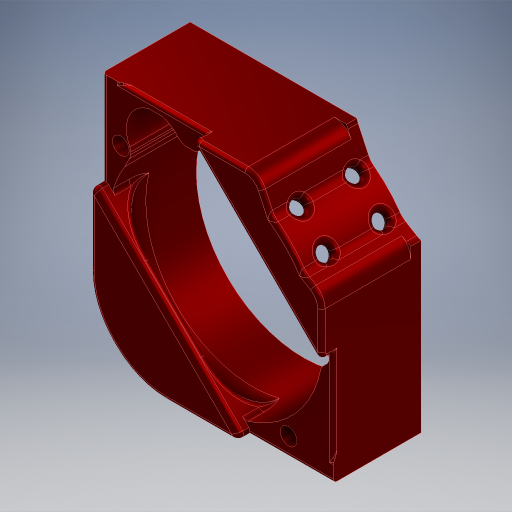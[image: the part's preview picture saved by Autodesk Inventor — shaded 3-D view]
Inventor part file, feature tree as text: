
AUTODESK INVENTOR PART (.ipt)
format: ipt  version: 2024.2 (Build 282272000, 272)  size: 4,199,424 bytes
history: native  units: in
note: dims shown in document units (in); Inventor stores cm internally (conversion verified against a paired STEP export)
features: extrude x10, sketch x10, fillet x3, projected_geometry x1
ambient origin geometry x8: Origin, YZ Plane, XZ Plane, XY Plane, X Axis, Y Axis, Z Axis, Center Point
bodies: Solid1 (feature_tree)
feature tree (24):
  extrude  "Extrusion1"  Depth=0.3937in TaperAngle=0.0deg
  extrude  "Extrusion2"  Depth=0.0591in TaperAngle=0.0deg
  extrude  "Extrusion3"  Depth=0.3937in
  extrude  "Extrusion4"  Depth=0.2313in TaperAngle=0.0deg
  extrude  "Extrusion5"  Depth=0.0013in
  extrude  "Extrusion6"  Depth=0.0197in
  extrude  "Extrusion7"  Depth=7.0034in TaperAngle=0.0deg
  extrude  "Extrusion8"  Depth=1.9685in
  extrude  "Extrusion9"  [1 undecoded]
  fillet  "Fillet3"  [1 undecoded]
  fillet  "Fillet4"  [1 undecoded]
  extrude  "Extrusion10"  [1 undecoded]
  sketch  "Sketch1"  dims[d0=0.3937in d1=0.0in d2=0.3937in d3=0.0in]
  sketch  "Sketch2"  dims[d4=0.0591in d5=0.0in d8=0.0591in d9=0.0in]
  sketch  "Sketch3"  dims[d11=0.3937in d12=0.0in d13=0.1772in]
  sketch  "Sketch4"  dims[d14=0.2313in d15=0.0in d16=0.2313in d17=0.0in]
  sketch  "Sketch5"  dims[d18=0.2313in d19=0.0in d21=0.0013in]
  sketch  "Sketch6"  dims[d22=0.2313in d23=0.0in d24=0.0197in]
  projected_geometry  "Projected Loop1"
  sketch  "Sketch7"  dims[d25=0.0197in d26=7.0034in d27=0.0in]
  sketch  "Sketch8"  dims[d6=0.0197in d7=1.9685in]
  sketch  "Sketch9"
  sketch  "Sketch10"
  fillet  "Fillet21"  [1 undecoded]
note: 5 required parameter values undecoded (feature->parameter linkage not recoverable at this tier; creation-order binding heuristic only, values carry confidence <= 0.55)
